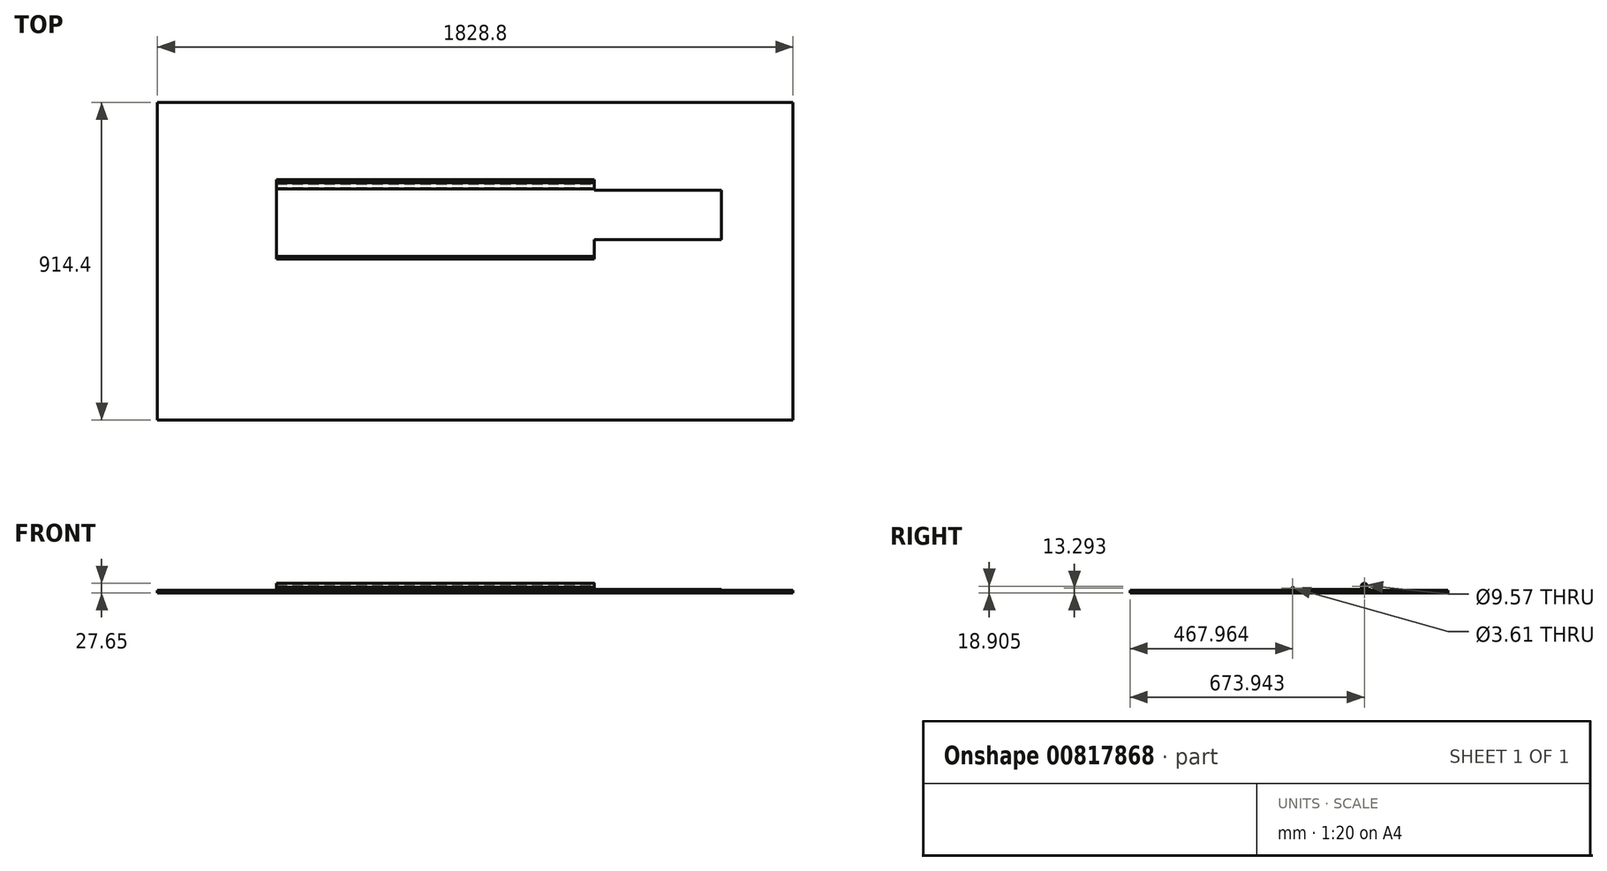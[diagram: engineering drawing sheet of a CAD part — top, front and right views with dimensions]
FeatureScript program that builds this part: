
annotation { "Feature Type Name" : "Feature", "Feature Type Description" : "" }
export const myFeature = defineFeature(function(context is Context, id is Id, definition is map)
    precondition{}
    {
        {
            var Q0;
            Q0=qCreatedBy(makeId("Top.planeOp"),FACE);
            var sketch = newSketch(context, id + "F0", { "sketchPlane" : qUnion([Q0])});
            skLineSegment(sketch, "E0.bottom", {"start": v(-140.64, 859.73) * mm, "end": v(1688.16, 859.73) * mm});
            skLineSegment(sketch, "E0.top", {"start": v(-140.64, -54.67) * mm, "end": v(1688.16, -54.67) * mm});
            skLineSegment(sketch, "E0.left", {"start": v(-140.64, 859.73) * mm, "end": v(-140.64, -54.67) * mm});
            skLineSegment(sketch, "E0.right", {"start": v(1688.16, 859.73) * mm, "end": v(1688.16, -54.67) * mm});
            skSolve(sketch);
        }
        {
            assignVariable(context, id + "F1", {"name" : "boardThickness", "anyValue" : 7.62 * mm});
        }
        {
            var Q0;
            Q0=makeQuery(id+"F0.imprint","IMPRINT",FACE,{"disambiguationData":[TD([[makeQuery(id+"F0.imprint","IMPRINT",EDGE,{"derivedFrom":sQuery(id+"F0.wireOp",EDGE,"E0.bottom")}),-1.0]])]});
            extrude(context, id + "F2", {"entities" : qUnion([Q0]), "oppositeDirection" : true, "depth" : getVariable(context, 'boardThickness'), "offsetDistance" : 25.4 * mm});
        }
        {
            var Q0;
            Q0=qCreatedBy(makeId("Top.planeOp"),FACE);
            var sketch = newSketch(context, id + "F3", { "sketchPlane" : qUnion([Q0])});
            skLineSegment(sketch, "E1.bottom", {"start": v(-826.97, 78.64) * mm, "end": v(87.43, 78.64) * mm});
            skLineSegment(sketch, "E1.top", {"start": v(-826.97, -149.96) * mm, "end": v(87.43, -149.96) * mm});
            skLineSegment(sketch, "E1.left", {"start": v(-826.97, 78.64) * mm, "end": v(-826.97, -149.96) * mm});
            skLineSegment(sketch, "E1.right", {"start": v(87.43, 78.64) * mm, "end": v(87.43, -149.96) * mm});
            skLineSegment(sketch, "E2.bottom", {"start": v(87.43, -94.64) * mm, "end": v(453.19, -94.64) * mm});
            skLineSegment(sketch, "E2.top", {"start": v(87.43, 48.05) * mm, "end": v(453.19, 48.05) * mm});
            skLineSegment(sketch, "E2.left", {"start": v(87.43, -94.64) * mm, "end": v(87.43, 48.05) * mm});
            skLineSegment(sketch, "E2.right", {"start": v(453.19, -94.64) * mm, "end": v(453.19, 48.05) * mm});
            skSolve(sketch);
        }
        {
            var Q0;
            {var subQ1=sQuery(id+"F3.wireOp",EDGE,"E1.bottom");Q0=makeQuery(id+"F3.imprint","IMPRINT",FACE,{"disambiguationData":[TD([[makeQuery(id+"F3.imprint","IMPRINT",EDGE,{"derivedFrom":subQ1}),-1.0]])]});}
            var Q1;
            Q1=makeQuery(id+"F3.imprint","IMPRINT",FACE,{"disambiguationData":[TD([[makeQuery(id+"F3.imprint","IMPRINT",EDGE,{"derivedFrom":sQuery(id+"F3.wireOp",EDGE,"E2.bottom")}),1.0]])]});
            extrude(context, id + "F4", {"entities" : qUnion([Q0, Q1]), "oppositeDirection" : true, "depth" : getVariable(context, 'boardThickness'), "offsetDistance" : 25.4 * mm});
        }
        {
            var Q0;
            Q0=makeQuery(id+"F4.opExtrude","SWEPT_BODY",BODY,{"disambiguationData":[OSD([sQuery(id+"F3.wireOp",EDGE,"E1.bottom"),sQuery(id+"F3.wireOp",EDGE,"E1.top"),sQuery(id+"F3.wireOp",EDGE,"E1.left"),sQuery(id+"F3.wireOp",EDGE,"E1.right"),sQuery(id+"F3.wireOp",EDGE,"E2.bottom"),sQuery(id+"F3.wireOp",EDGE,"E2.top"),sQuery(id+"F3.wireOp",EDGE,"E2.right")])]});
            transform(context, id + "F5", {"entities" : qUnion([Q0]), "transformType" : TransformType.TRANSLATION_3D, "dx" : 1028.7 * mm, "dy" : 558.8 * mm, "dz" : 2.54 * mm, "makeCopy" : false});
        }
        {
            var Q0;
            {var subQ0=sQuery(id+"F3.wireOp",EDGE,"E1.right");Q0=makeQuery(id+"F4.opExtrude","SWEPT_FACE",FACE,{"disambiguationData":[OSD([subQ0]),TDD([makeQuery(id+"F3.imprint","IMPRINT",EDGE,{"disambiguationData":[TD([[makeQuery(id+"F3.imprint","INTERSECT",VERTEX,{"derivedFrom":[sQuery(id+"F3.wireOp",EDGE,"E1.top"),subQ0]}),1.0]])],"derivedFrom":subQ0})])]});}
            cPlane(context, id + "F6", {"entities" : qUnion([Q0]), "cplaneType" : CPlaneType.OFFSET, "offset" : 0 * mm, "width" : 152.4 * mm, "height" : 152.4 * mm});
        }
        {
            var Q0;
            Q0=qCreatedBy(id+"F6.planeOp",FACE);
            var sketch = newSketch(context, id + "F7", { "sketchPlane" : qUnion([Q0])});
            skCircle(sketch, "E3", {"center": v(413.3, 5.67) * mm, "radius": 3.13 * mm});
            skCircle(sketch, "E4", {"center": v(413.3, 5.67) * mm, "radius": 1.8 * mm});
            skSolve(sketch);
        }
        {
            var Q0;
            Q0=makeQuery(id+"F7.imprint","IMPRINT",FACE,{"disambiguationData":[TD([[makeQuery(id+"F7.imprint","IMPRINT",EDGE,{"derivedFrom":sQuery(id+"F7.wireOp",EDGE,"E3")}),1.0]])]});
            var Q1;
            Q1=makeQuery(id+"F4.opExtrude","SWEPT_FACE",FACE,{"disambiguationData":[OSD([sQuery(id+"F3.wireOp",EDGE,"E1.left")])]});
            extrude(context, id + "F8", {"entities" : qUnion([Q0]), "operationType" : NewBodyOperationType.ADD, "endBound" : BoundingType.UP_TO_SURFACE, "oppositeDirection" : true, "depth" : 25.4 * mm, "endBoundEntityFace" : qUnion([Q1]), "offsetDistance" : 25.4 * mm});
        }
        {
            var Q0;
            {var subQ0=sQuery(id+"F3.wireOp",EDGE,"E1.right");Q0=makeQuery(id+"F4.opExtrude","SWEPT_FACE",FACE,{"disambiguationData":[OSD([subQ0]),TDD([makeQuery(id+"F3.imprint","IMPRINT",EDGE,{"disambiguationData":[TD([[makeQuery(id+"F3.imprint","INTERSECT",VERTEX,{"derivedFrom":[sQuery(id+"F3.wireOp",EDGE,"E1.bottom"),subQ0]}),-1.0]])],"derivedFrom":subQ0})])]});}
            cPlane(context, id + "F9", {"entities" : qUnion([Q0]), "cplaneType" : CPlaneType.OFFSET, "offset" : 0 * mm, "width" : 152.4 * mm, "height" : 152.4 * mm});
        }
        {
            var Q0;
            Q0=qCreatedBy(id+"F9.planeOp",FACE);
            var sketch = newSketch(context, id + "F10", { "sketchPlane" : qUnion([Q0])});
            skCircle(sketch, "E5", {"center": v(619.27, 11.28) * mm, "radius": 8.74 * mm});
            skCircle(sketch, "E6", {"center": v(619.27, 11.28) * mm, "radius": 4.78 * mm});
            skSolve(sketch);
        }
        {
            var Q0;
            Q0=makeQuery(id+"F10.imprint","IMPRINT",FACE,{"disambiguationData":[TD([[makeQuery(id+"F10.imprint","IMPRINT",EDGE,{"derivedFrom":sQuery(id+"F10.wireOp",EDGE,"E5")}),1.0]])]});
            var Q1;
            Q1=makeQuery(id+"F4.opExtrude","SWEPT_FACE",FACE,{"disambiguationData":[OSD([sQuery(id+"F3.wireOp",EDGE,"E1.left")])]});
            extrude(context, id + "F11", {"entities" : qUnion([Q0]), "operationType" : NewBodyOperationType.ADD, "endBound" : BoundingType.UP_TO_SURFACE, "oppositeDirection" : true, "depth" : 25.4 * mm, "endBoundEntityFace" : qUnion([Q1]), "offsetDistance" : 25.4 * mm});
        }
        {
            var Q0;
            Q0=makeQuery(id+"F4.opExtrude","CAP_FACE",FACE,{"disambiguationData":[OSD([sQuery(id+"F3.wireOp",EDGE,"E1.bottom"),sQuery(id+"F3.wireOp",EDGE,"E1.top"),sQuery(id+"F3.wireOp",EDGE,"E1.left"),sQuery(id+"F3.wireOp",EDGE,"E1.right"),sQuery(id+"F3.wireOp",EDGE,"E2.bottom"),sQuery(id+"F3.wireOp",EDGE,"E2.top"),sQuery(id+"F3.wireOp",EDGE,"E2.right")])],"isStart":true});
            var sketch = newSketch(context, id + "F12", { "sketchPlane" : qUnion([Q0])});
            skLineSegment(sketch, "E7", {"start": v(273.65, 583.34) * mm, "end": v(394.05, 540.05) * mm});
            skLineSegment(sketch, "E8", {"start": v(394.05, 540.05) * mm, "end": v(394.05, 577.93) * mm});
            skLineSegment(sketch, "E9", {"start": v(262.83, 464.3) * mm, "end": v(394.05, 491.35) * mm});
            skLineSegment(sketch, "E10", {"start": v(394.05, 491.35) * mm, "end": v(394.05, 453.47) * mm});
            skLineSegment(sketch, "E11", {"start": v(628.95, 584.71) * mm, "end": v(685.2, 558.87) * mm});
            skLineSegment(sketch, "E12", {"start": v(679.13, 481.33) * mm, "end": v(610.7, 450.92) * mm});
            skSolve(sketch);
        }
        {
            var Q0;
            {var subQ1=sQuery(id+"F3.wireOp",EDGE,"E1.bottom");Q0=makeQuery(id+"F12.imprint","IMPRINT",FACE,{"disambiguationData":[TD([[makeQuery(id+"F12.imprint","IMPRINT",EDGE,{"derivedFrom":makeQuery(id+"F4.opExtrude","CAP_EDGE",EDGE,{"disambiguationData":[OSD([subQ1])],"isStart":true})}),-1.0]])]});}
            var Q1;
            Q1=sQuery(id+"F12.wireOp",EDGE,"E7");
            var Q2;
            Q2=sQuery(id+"F12.wireOp",EDGE,"E8");
            var Q3;
            Q3=sQuery(id+"F12.wireOp",EDGE,"E9");
            var Q4;
            Q4=sQuery(id+"F12.wireOp",EDGE,"E10");
            var Q5;
            Q5=sQuery(id+"F12.wireOp",EDGE,"E12");
            var Q6;
            Q6=sQuery(id+"F12.wireOp",EDGE,"E11");
            extrude(context, id + "F13", {"entities" : qUnion([Q0]), "bodyType" : ToolBodyType.SURFACE, "surfaceEntities" : qUnion([Q1, Q2, Q3, Q4, Q5, Q6]), "depth" : 50.8 * mm, "offsetDistance" : 25.4 * mm});
        }
    });
